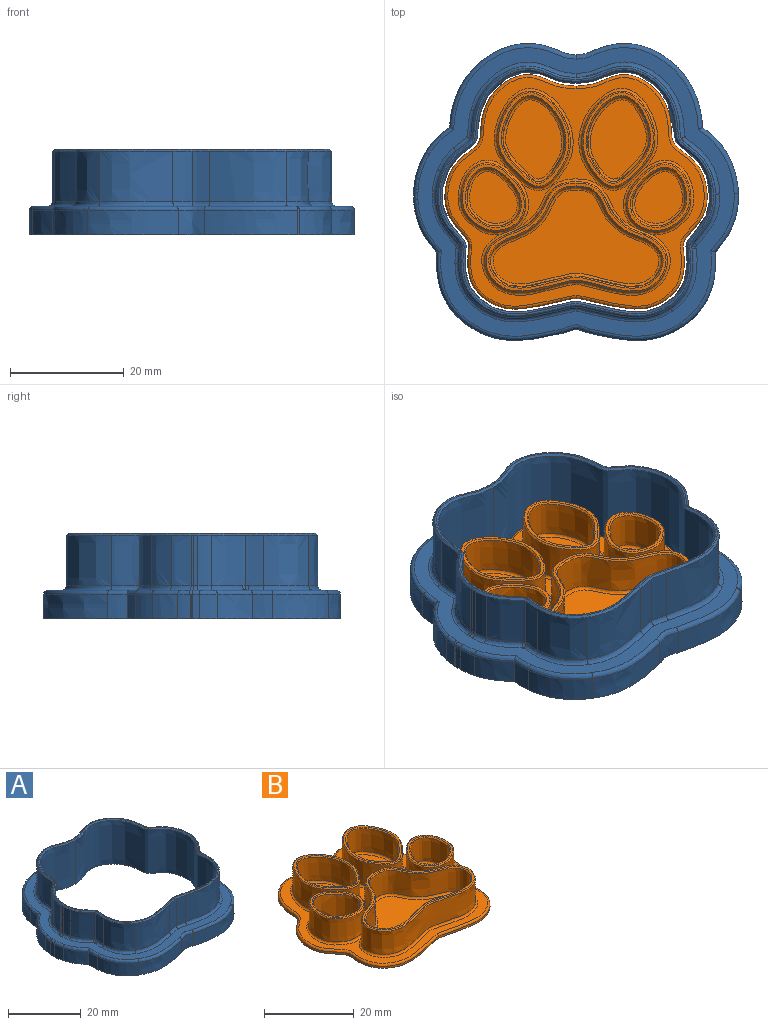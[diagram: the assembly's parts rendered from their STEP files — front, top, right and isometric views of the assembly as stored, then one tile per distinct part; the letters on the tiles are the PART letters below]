
ASSEMBLY  parts=2 mates=1
PART A: 111 faces, bbox 57.5x52.6x15.4 mm
  f0: extruded ~8.9x2.52mm, area 29mm2, adj f1,f16,f48,f91
  f1: extruded ~8.9x4.92mm, area 44.6mm2, adj f0,f2,f50,f89
  f2: extruded ~17.75x8.9mm, area 194mm2, adj f1,f3,f52,f88
  f3: extruded ~18.44x12.69mm, area 237.7mm2, adj f2,f4,f54,f90
  f4: extruded ~9.75x8.9mm, area 106.6mm2, adj f3,f5,f56,f92
  f5: extruded ~9.1x8.9mm, area 91.8mm2, adj f4,f6,f58,f94,f107
  f6: extruded ~10.82x8.9mm, area 108.5mm2, adj f5,f7,f60,f97,f108
  f7: extruded ~13.41x8.9mm, area 123.6mm2, adj f6,f8,f62,f99
  f8: extruded ~8.9x3.09mm, area 28.1mm2, adj f7,f9,f64,f101
  f9: extruded ~8.9x3.35mm, area 30.5mm2, adj f8,f10,f63,f103
  f10: extruded ~12.81x8.9mm, area 117.6mm2, adj f9,f11,f61,f104
  f11: extruded ~8.9x7.92mm, area 84.3mm2, adj f10,f12,f59,f106
  f12: extruded ~8.9x3.2mm, area 28.6mm2, adj f11,f13,f57,f105,f109
  f13: extruded ~8.9x6.03mm, area 64.2mm2, adj f12,f14,f55,f102,f110
  f14: extruded ~8.9x2.32mm, area 20.9mm2, adj f13,f17,f53,f100
  f15: extruded ~8.9x3.47mm, area 31.9mm2, adj f16,f18,f47,f95
  f16: extruded ~8.9x3.53mm, area 39.2mm2, adj f0,f15,f46,f93
  f17: extruded ~8.9x0.79mm, area 7mm2, adj f14,f18,f51,f98
  f18: extruded ~8.9x0.42mm, area 3.8mm2, adj f15,f17,f49,f96
  f19: extruded ~42.08x23.5mm, area 1091.5mm2, adj f20,f22,f65
  f20: extruded ~42.08x23.5mm, area 1091.5mm2, adj f19,f22,f66
  f21: plane 48.77x44mm, normal (0,0,1), area 52.6mm2, adj f46,f47,f48,f49,f50,f51,f52,f53
  f22: plane 57.02x52.14mm, normal (0,0,-1), area 828.2mm2, adj f19,f20,f23,f24,f25,f26,f27,f28
  f23: extruded ~9.75x6.13mm, area 50.8mm2, adj f22,f24,f44,f70
  f24: extruded ~4.25x3.6mm, area 15.3mm2, adj f22,f23,f25,f68
  f25: extruded ~6.16x4.25mm, area 30.6mm2, adj f22,f24,f26,f67
  f26: extruded ~4.25x3.12mm, area 13.4mm2, adj f22,f25,f27,f69
  f27: extruded ~4.25x1.23mm, area 5.2mm2, adj f22,f26,f28,f71
  f28: plane 4.25x0.33mm, normal (-1,0.06,0), area 1.4mm2, adj f22,f27,f29,f73
  f29: extruded ~4.31x0.4mm, area 0.8mm2, adj f22,f28,f30,f73,f75
  f30: extruded ~4.25x2.4mm, area 10.3mm2, adj f22,f29,f31,f75
  f31: extruded ~4.51x4.25mm, area 20.7mm2, adj f22,f30,f32,f77
  f32: extruded ~4.25x2.99mm, area 16.5mm2, adj f22,f31,f33,f79
  f33: extruded ~4.25x1.76mm, area 9.5mm2, adj f22,f32,f34,f81
  f34: plane 4.25x0.01mm, normal (-1,0.06,0), area 0mm2, adj f22,f33,f35,f83
  f35: extruded ~4.25x3.41mm, area 14.7mm2, adj f22,f34,f36,f85
  f36: extruded ~21.72x11.29mm, area 116.6mm2, adj f22,f35,f37,f87
  f37: extruded ~22.2x14.72mm, area 131.6mm2, adj f22,f36,f38,f86
  f38: extruded ~11.55x6.3mm, area 58mm2, adj f22,f37,f39,f84
  f39: extruded ~10.33x4.25mm, area 48.6mm2, adj f22,f38,f40,f82
  f40: extruded ~12.99x5.68mm, area 63.3mm2, adj f22,f39,f41,f80
  f41: plane 4.25x0.24mm, normal (0.55,-0.83,0), area 1.2mm2, adj f22,f40,f42,f78
  f42: extruded ~16.42x4.25mm, area 72.3mm2, adj f22,f41,f43,f76
  f43: extruded ~4.6x4.25mm, area 20.5mm2, adj f22,f42,f44,f74
  f44: extruded ~15.83x4.25mm, area 69.5mm2, adj f22,f23,f43,f72
  f45: plane 55.57x50.7mm, normal (0,0,1), area 422mm2, adj f67,f68,f69,f70,f71,f72,f73,f74
  f46: bspline ~3.66x2.79mm, area 2.1mm2, adj f16,f21,f47,f48
  f47: bspline ~3.5x1.18mm, area 1.7mm2, adj f15,f21,f46,f49
  f48: bspline ~2.81x2.33mm, area 1.6mm2, adj f0,f21,f46,f50
  f49: bspline ~0.44x0.38mm, area 0.2mm2, adj f18,f21,f47,f51
  f50: bspline ~5.12x1.12mm, area 2.5mm2, adj f1,f21,f48,f52
  f51: bspline ~0.79x0.37mm, area 0.4mm2, adj f17,f21,f49,f53
  f52: bspline ~18.86x8.01mm, area 10.7mm2, adj f2,f21,f50,f54
  f53: bspline ~2.33x0.67mm, area 1.1mm2, adj f14,f21,f51,f55
  f54: bspline ~19.79x12.89mm, area 13.1mm2, adj f3,f21,f52,f56
  f55: bspline ~6.12x4.19mm, area 3.6mm2, adj f13,f21,f53,f57
  f56: bspline ~9.77x6.38mm, area 5.9mm2, adj f4,f21,f54,f58
  f57: bspline ~3.3x0.59mm, area 1.6mm2, adj f12,f21,f55,f59
  f58: bspline ~9.1x4.58mm, area 5.1mm2, adj f5,f21,f56,f60
  f59: bspline ~7.93x4.52mm, area 4.6mm2, adj f11,f21,f57,f61
  f60: bspline ~10.86x4.2mm, area 6mm2, adj f6,f21,f58,f62
  f61: bspline ~12.81x1.9mm, area 6.5mm2, adj f10,f21,f59,f63
  f62: bspline ~13.41x2.11mm, area 6.8mm2, adj f7,f21,f60,f64
  f63: bspline ~3.61x1.03mm, area 1.7mm2, adj f9,f21,f61,f64
  f64: bspline ~3.33x0.96mm, area 1.6mm2, adj f8,f21,f62,f63
  f65: bspline ~42.93x25.97mm, area 37.4mm2, adj f19,f21,f66
  f66: bspline ~42.92x25.92mm, area 37.4mm2, adj f20,f21,f65
  f67: bspline ~8.86x5.29mm, area 8.5mm2, adj f25,f45,f68,f69
  f68: bspline ~5.08x0.95mm, area 4.4mm2, adj f24,f45,f67,f70
  f69: bspline ~4.27x1.36mm, area 3.7mm2, adj f26,f45,f67,f71
  f70: bspline ~12.53x8.24mm, area 13.8mm2, adj f23,f45,f68,f72
  f71: bspline ~1.63x0.77mm, area 1.4mm2, adj f27,f45,f69,f73
  f72: bspline ~18.23x3.5mm, area 19mm2, adj f44,f45,f70,f74
  f73: cylinder r=0.75mm len=0.78mm, axis (-0.06,-1,0), area 0.6mm2, adj f28,f29,f45,f71,f75
  f74: bspline ~6.05x1.65mm, area 5.8mm2, adj f43,f45,f72,f76
  f75: bspline ~2.99x1.12mm, area 2.3mm2, adj f29,f30,f45,f73,f77
  f76: bspline ~21.28x5.86mm, area 19.7mm2, adj f42,f45,f74,f78
  f77: bspline ~5.8x2.77mm, area 5.6mm2, adj f31,f45,f75,f79
  f78: cylinder r=0.75mm len=0.79mm, axis (0.83,0.55,0), area 0.3mm2, adj f41,f45,f76,f80
  f79: bspline ~4.05x3.49mm, area 4.5mm2, adj f32,f45,f77,f81
  f80: bspline ~16.2x9.85mm, area 17.4mm2, adj f40,f45,f78,f82
  f81: bspline ~3.86x3.25mm, area 2.8mm2, adj f33,f45,f79,f83
  f82: bspline ~20.39x11.19mm, area 13.4mm2, adj f39,f45,f80,f84
  f83: cylinder r=0.75mm len=0.77mm, axis (-0.06,-1,0), area 0.2mm2, adj f34,f45,f81,f85
  f84: bspline ~13.59x7.97mm, area 16mm2, adj f38,f45,f82,f86
  f85: bspline ~14.1x2.78mm, area 4mm2, adj f35,f45,f83,f87
  f86: bspline ~26.28x15.73mm, area 36.2mm2, adj f37,f45,f84,f87
  f87: bspline ~24.43x20.21mm, area 32mm2, adj f36,f45,f85,f86
  f88: bspline ~23.52x15.68mm, area 26.1mm2, adj f2,f45,f89,f90
  f89: bspline ~7.38x2.15mm, area 5.8mm2, adj f1,f45,f88,f91
  f90: bspline ~20.77x14.67mm, area 31.8mm2, adj f3,f45,f88,f92
  f91: bspline ~3.48x3.03mm, area 3.8mm2, adj f0,f45,f89,f93
  f92: bspline ~11.33x7.1mm, area 14.2mm2, adj f4,f45,f90,f94
  f93: bspline ~8.48x8.29mm, area 5.3mm2, adj f16,f45,f91,f95
  f94: bspline ~9.52x4.69mm, area 11.6mm2, adj f5,f45,f92,f107
  f95: bspline ~4.99x1.92mm, area 4.3mm2, adj f15,f45,f93,f96
  f96: bspline ~0.79x0.75mm, area 0.5mm2, adj f18,f45,f95,f98
  f97: bspline ~12.37x6.66mm, area 14.1mm2, adj f6,f45,f99,f108
  f98: bspline ~2.11x0.78mm, area 1mm2, adj f17,f45,f96,f100
  f99: bspline ~19.18x4.15mm, area 16.6mm2, adj f7,f45,f97,f101
  f100: bspline ~3.36x1.21mm, area 2.9mm2, adj f14,f45,f98,f102
  f101: bspline ~4.74x1.65mm, area 3.6mm2, adj f8,f45,f99,f103
  f102: bspline ~8.63x5.06mm, area 8mm2, adj f13,f45,f100,f110
  f103: bspline ~5.42x1.74mm, area 4mm2, adj f9,f45,f101,f104
  f104: bspline ~18.56x3.86mm, area 15.8mm2, adj f10,f45,f103,f106
  f105: bspline ~4.3x0.93mm, area 3.2mm2, adj f12,f45,f106,f109
  f106: bspline ~18.88x7.22mm, area 11.5mm2, adj f11,f45,f104,f105
  f107: bspline ~0.9x0.75mm, area 0.6mm2, adj f5,f45,f94,f108
  f108: bspline ~0.77x0.75mm, area 0.5mm2, adj f6,f45,f97,f107
  f109: bspline ~0.77x0.75mm, area 0.6mm2, adj f12,f45,f105,f110
  f110: bspline ~0.89x0.75mm, area 0.5mm2, adj f13,f45,f102,f109
PART B: 46 faces, bbox 46.8x41.9x8.3 mm
  f0: plane 45.03x40.14mm, normal (0,0,1), area 361.1mm2, adj f24,f25,f26,f27,f28,f34,f35
  f1: extruded ~41.08x23.01mm, area 36.6mm2, adj f2,f3,f35
  f2: extruded ~41.08x23.01mm, area 36.6mm2, adj f1,f3,f34
  f3: plane 46.48x41.6mm, normal (0,0,-1), area 1489.4mm2, adj f1,f2
  f4: extruded ~29.81x17.37mm, area 484.3mm2, adj f33,f41
  f5: extruded ~31.74x19.36mm, area 532.8mm2, adj f26,f40
  f6: plane 31.8x18.97mm, normal (0,0,1), area 44.3mm2, adj f40,f41
  f7: plane 29.1x16.43mm, normal (0,0,1), area 283.3mm2, adj f33
  f8: extruded ~14.88x10.85mm, area 246.4mm2, adj f32,f39
  f9: extruded ~16.87x12.84mm, area 286.6mm2, adj f24,f38
  f10: plane 16.54x12.54mm, normal (0,0,1), area 21.3mm2, adj f38,f39
  f11: plane 13.89x9.86mm, normal (0,0,1), area 98.2mm2, adj f32
  f12: extruded ~16.87x12.84mm, area 286.6mm2, adj f27,f42
  f13: extruded ~14.88x10.85mm, area 246.4mm2, adj f31,f43
  f14: plane 16.81x12.82mm, normal (0,0,1), area 21.7mm2, adj f42,f43
  f15: plane 13.89x9.86mm, normal (0,0,1), area 98.2mm2, adj f31
  f16: extruded ~12.03x11.33mm, area 228.4mm2, adj f25,f36
  f17: extruded ~10.05x9.33mm, area 189.3mm2, adj f30,f37
  f18: plane 11.67x10.98mm, normal (0,0,1), area 16.5mm2, adj f36,f37
  f19: plane 9.09x8.34mm, normal (0,0,1), area 56.9mm2, adj f30
  f20: extruded ~10.05x9.33mm, area 189.3mm2, adj f29,f45
  f21: extruded ~12.03x11.33mm, area 228.4mm2, adj f28,f44
  f22: plane 11.67x10.97mm, normal (0,0,1), area 16.6mm2, adj f44,f45
  f23: plane 9.09x8.34mm, normal (0,0,1), area 56.9mm2, adj f29
  f24: bspline ~17.9x13.87mm, area 36.7mm2, adj f0,f9,f25
  f25: bspline ~13.07x12.34mm, area 29.6mm2, adj f0,f16,f24,f26
  f26: bspline ~32.99x20.39mm, area 66.8mm2, adj f0,f5,f25,f28
  f27: bspline ~17.9x13.86mm, area 36.8mm2, adj f0,f12,f28
  f28: bspline ~13.09x12.34mm, area 29.6mm2, adj f0,f21,f26,f27
  f29: bspline ~10.09x9.34mm, area 22.9mm2, adj f20,f23
  f30: bspline ~10.09x9.35mm, area 22.9mm2, adj f17,f19
  f31: bspline ~14.89x10.87mm, area 30.1mm2, adj f13,f15
  f32: bspline ~14.89x10.87mm, area 30.1mm2, adj f8,f11
  f33: bspline ~30.1x17.43mm, area 60mm2, adj f4,f7
  f34: bspline ~41.15x38.97mm, area 57.3mm2, adj f0,f2,f35
  f35: bspline ~41.15x38.97mm, area 57.3mm2, adj f0,f1,f34
  f36: bspline ~12.2x11.4mm, area 12.6mm2, adj f16,f18
  f37: bspline ~10.68x9.88mm, area 11mm2, adj f17,f18
  f38: bspline ~16.96x12.93mm, area 15.9mm2, adj f9,f10
  f39: bspline ~15.49x11.42mm, area 14.3mm2, adj f8,f10
  f40: bspline ~32.19x19.46mm, area 29.4mm2, adj f5,f6
  f41: bspline ~30.7x17.96mm, area 28.1mm2, adj f4,f6
  f42: bspline ~17x12.88mm, area 15.9mm2, adj f12,f14
  f43: bspline ~15.49x11.46mm, area 14.2mm2, adj f13,f14
  f44: bspline ~12.2x11.39mm, area 12.6mm2, adj f21,f22
  f45: bspline ~10.69x9.89mm, area 11mm2, adj f20,f22
PLACE A t=(-19.2,4.14,-12.35)mm
PLACE B t=(-19.21,4.17,-12.35)mm
MATE fastened B.f3 <-> A.f22  axis (0,0,-1) through (-19.21,-13.16,-12.35)mm
